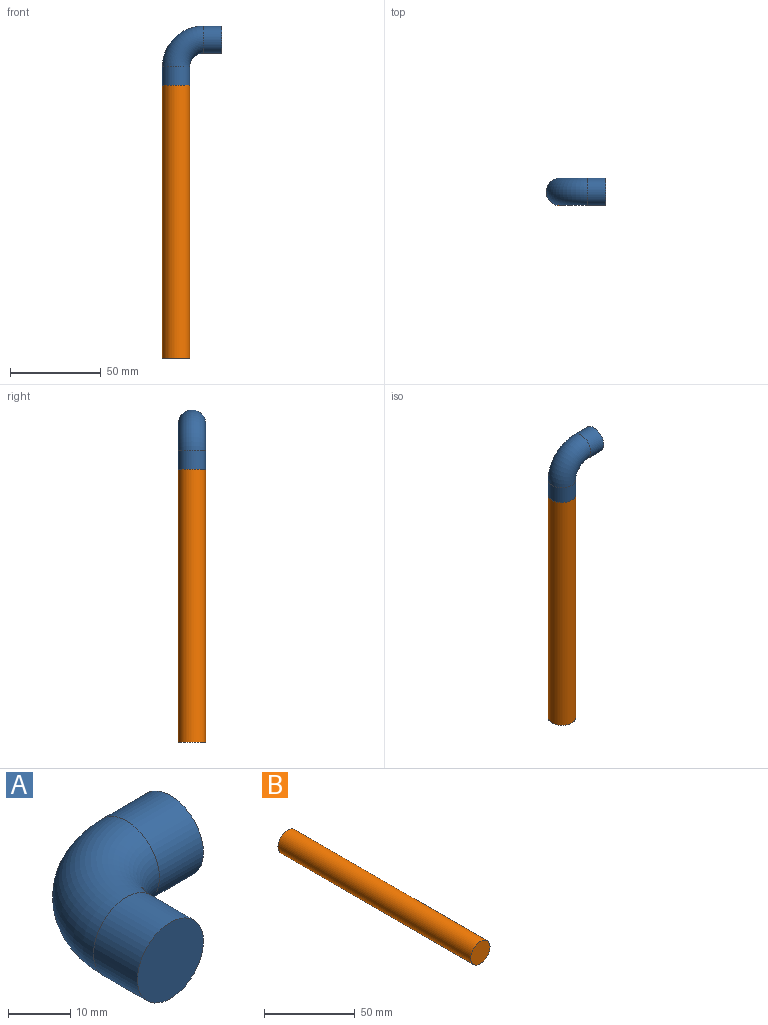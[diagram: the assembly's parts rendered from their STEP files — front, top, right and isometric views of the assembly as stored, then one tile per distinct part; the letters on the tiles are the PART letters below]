
ASSEMBLY  parts=2 mates=1
PART A: 5 faces, bbox 34.4x34.4x15 mm
  f0: plane 15x15mm, normal (0,-1,0), area 176.7mm2, adj f2
  f1: plane 15x15mm, normal (1,0,0), area 176.7mm2, adj f4
  f2: cylinder r=7.5mm len=15mm, axis (0,1,0), area 471.2mm2, adj f0,f3
  f3: torus R=15mm, axis (0,0,-1), area 1110.3mm2, adj f2,f4
  f4: cylinder r=7.5mm len=15mm, axis (1,0,0), area 471.2mm2, adj f1,f3
PART B: 3 faces, bbox 15x150x15 mm
  f0: cylinder r=7.5mm len=150mm, axis (0,1,0), area 7068.6mm2, adj f1,f2
  f1: plane 15x15mm, normal (0,-1,0), area 176.7mm2, adj f0
  f2: plane 15x15mm, normal (0,1,0), area 176.7mm2, adj f0
PLACE A rot(axis=(1,0,0),90deg) t=(3801.56,7450.29,-1350)mm
PLACE B rot(axis=(1,0,0),90deg) t=(3863,7486.88,-1350)mm
MATE fastened A.f2 <-> B.f0  axis (0,0,-1) through (3801.56,7450.29,-1350)mm
